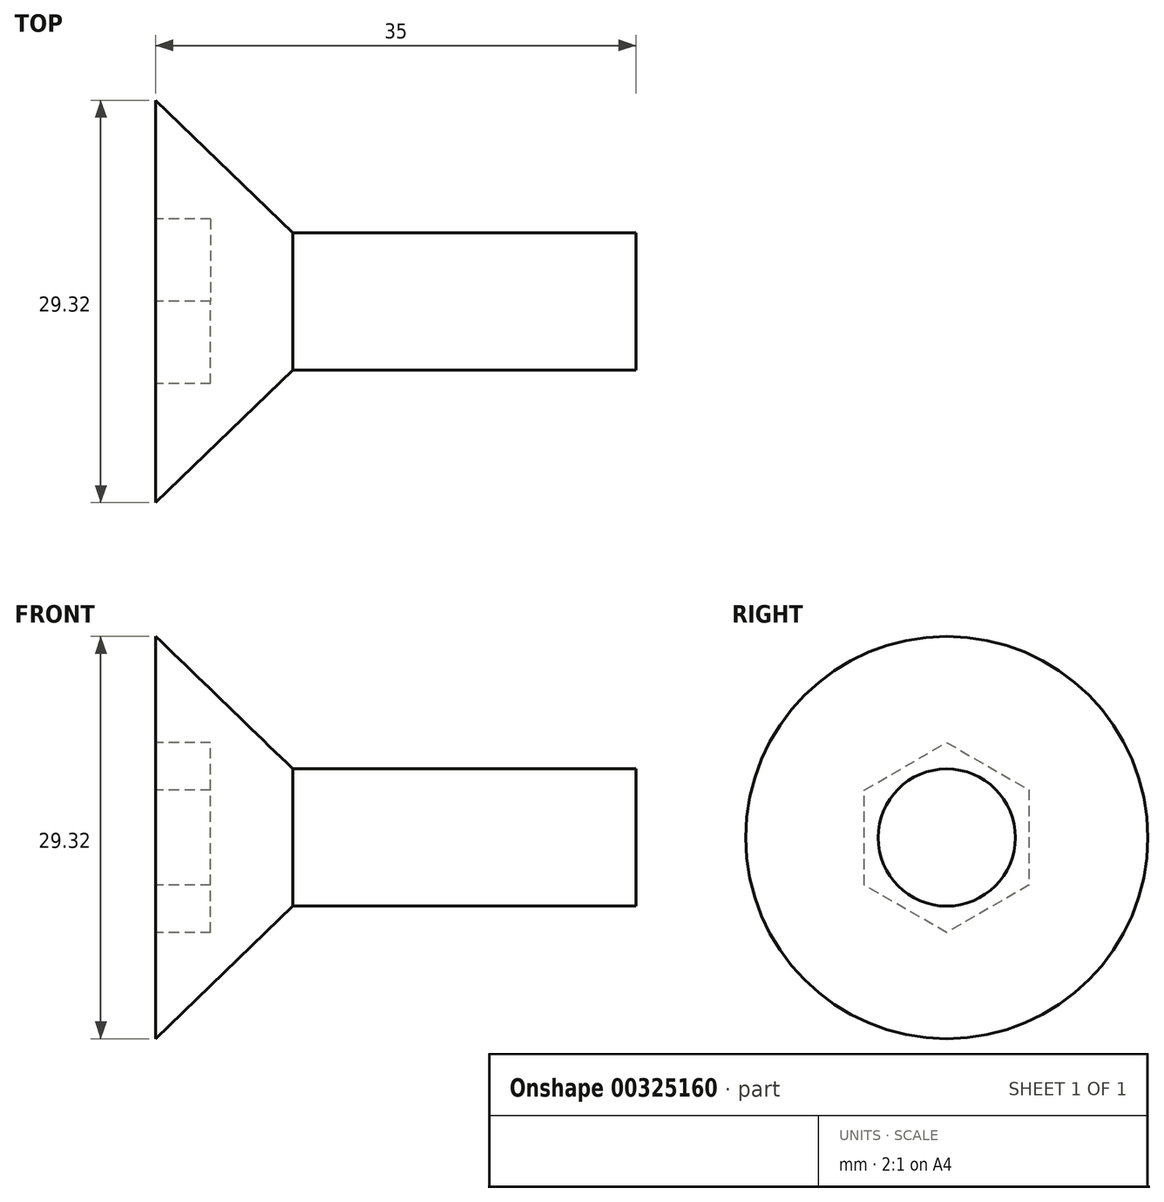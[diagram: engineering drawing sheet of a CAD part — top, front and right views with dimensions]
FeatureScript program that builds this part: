
annotation { "Feature Type Name" : "Feature", "Feature Type Description" : "" }
export const myFeature = defineFeature(function(context is Context, id is Id, definition is map)
    precondition{}
    {
        {
            var Q0;
            Q0=qCreatedBy(makeId("Front.planeOp"),FACE);
            var sketch = newSketch(context, id + "F0", { "sketchPlane" : qUnion([Q0])});
            skLineSegment(sketch, "E0", {"start": v(0, 0) * mm, "end": v(35, 0) * mm});
            skLineSegment(sketch, "E1", {"start": v(0, 0) * mm, "end": v(0, 14.66) * mm});
            skLineSegment(sketch, "E2", {"start": v(0, 14.66) * mm, "end": v(10, 5) * mm});
            skLineSegment(sketch, "E3", {"start": v(10, 5) * mm, "end": v(35, 5) * mm});
            skLineSegment(sketch, "E4", {"start": v(35, 5) * mm, "end": v(35, 0) * mm});
            skLineSegment(sketch, "E5", {"start": v(35, 0) * mm, "end": v(41.46, 0) * mm, "construction": true});
            skSolve(sketch);
        }
        {
            var Q0;
            Q0=makeQuery(id+"F0.imprint","IMPRINT",FACE,{"disambiguationData":[TD([[makeQuery(id+"F0.imprint","IMPRINT",EDGE,{"derivedFrom":sQuery(id+"F0.wireOp",EDGE,"E0")}),1.0]])]});
            var Q1;
            Q1=sQuery(id+"F0.wireOp",EDGE,"E0");
            revolve(context, id + "F1", {"entities" : qUnion([Q0]), "axis" : qUnion([Q1]), "revolveType" : RevolveType.FULL});
        }
        {
            var Q0;
            Q0=qCreatedBy(makeId("Right.planeOp"),FACE);
            var sketch = newSketch(context, id + "F2", { "sketchPlane" : qUnion([Q0])});
            skCircle(sketch, "E6.cCircle", {"center": v(0, 0) * mm, "radius": 6 * mm, "construction": true});
            skLineSegment(sketch, "E6.0", {"start": v(-6, 3.46) * mm, "end": v(0, 6.93) * mm});
            skLineSegment(sketch, "E6.1", {"start": v(0, 6.93) * mm, "end": v(6, 3.46) * mm});
            skLineSegment(sketch, "E6.2", {"start": v(6, 3.46) * mm, "end": v(6, -3.46) * mm});
            skLineSegment(sketch, "E6.3", {"start": v(6, -3.46) * mm, "end": v(0, -6.93) * mm});
            skLineSegment(sketch, "E6.4", {"start": v(0, -6.93) * mm, "end": v(-6, -3.46) * mm});
            skLineSegment(sketch, "E6.5", {"start": v(-6, -3.46) * mm, "end": v(-6, 3.46) * mm});
            skPoint(sketch, "E6.0.midPoint", {"position": v(-3, 5.2) * mm});
            skSolve(sketch);
        }
        {
            var Q0;
            Q0=makeQuery(id+"F2.imprint","IMPRINT",FACE,{"disambiguationData":[TD([[makeQuery(id+"F2.imprint","IMPRINT",EDGE,{"derivedFrom":sQuery(id+"F2.wireOp",EDGE,"E6.0")}),-1.0]])]});
            extrude(context, id + "F3", {"entities" : qUnion([Q0]), "operationType" : NewBodyOperationType.REMOVE, "depth" : 4 * mm});
        }
    });
